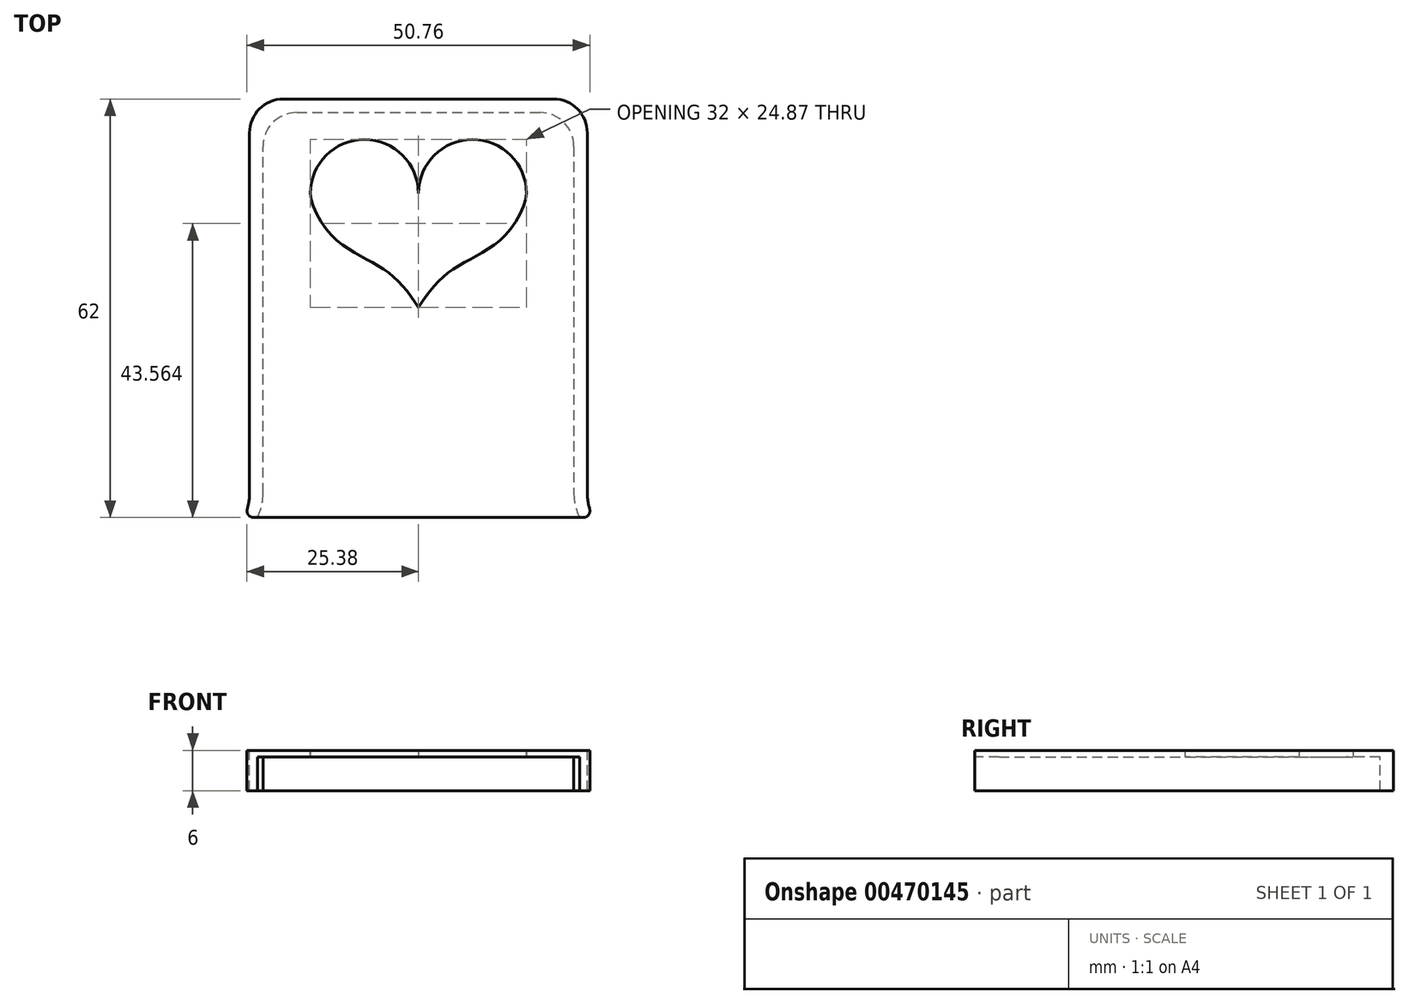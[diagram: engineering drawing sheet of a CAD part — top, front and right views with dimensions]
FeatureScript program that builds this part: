
annotation { "Feature Type Name" : "Feature", "Feature Type Description" : "" }
export const myFeature = defineFeature(function(context is Context, id is Id, definition is map)
    precondition{}
    {
        {
            var Q0;
            Q0=qCreatedBy(makeId("Top.planeOp"),FACE);
            var sketch = newSketch(context, id + "F0", { "sketchPlane" : qUnion([Q0])});
            skLineSegment(sketch, "E0", {"start": v(-23, 30) * mm, "end": v(23, 30) * mm});
            skLineSegment(sketch, "E1", {"start": v(23, 30) * mm, "end": v(23, -30) * mm});
            skLineSegment(sketch, "E2", {"start": v(23, -30) * mm, "end": v(-23, -30) * mm});
            skLineSegment(sketch, "E3", {"start": v(-23, -30) * mm, "end": v(-23, 30) * mm});
            skLineSegment(sketch, "E4", {"start": v(23, 30) * mm, "end": v(-23, -30) * mm, "construction": true});
            skLineSegment(sketch, "E5.MirrorCS", {"start": v(-25.5, -30) * mm, "end": v(-23, -20.3) * mm});
            skLineSegment(sketch, "E6.MirrorCS", {"start": v(-23, -30) * mm, "end": v(-25.5, -30) * mm});
            skLineSegment(sketch, "E7", {"start": v(0, 0) * mm, "end": v(0, 30) * mm, "construction": true});
            skLineSegment(sketch, "E8.MirrorCS", {"start": v(25.5, -30) * mm, "end": v(23, -20.3) * mm});
            skLineSegment(sketch, "E9.MirrorCS", {"start": v(23, -30) * mm, "end": v(25.5, -30) * mm});
            skSolve(sketch);
        }
        {
            var Q0;
            Q0=makeQuery(id+"F0.imprint","IMPRINT",FACE,{"disambiguationData":[TD([[makeQuery(id+"F0.imprint","IMPRINT",EDGE,{"derivedFrom":sQuery(id+"F0.wireOp",EDGE,"E0")}),-1.0]])]});
            var Q1;
            {var subQ2=sQuery(id+"F0.wireOp",EDGE,"E5.MirrorCS");Q1=makeQuery(id+"F0.imprint","IMPRINT",FACE,{"disambiguationData":[TD([[makeQuery(id+"F0.imprint","IMPRINT",EDGE,{"derivedFrom":subQ2}),-1.0]])]});}
            var Q2;
            {var subQ2=sQuery(id+"F0.wireOp",EDGE,"E8.MirrorCS");Q2=makeQuery(id+"F0.imprint","IMPRINT",FACE,{"disambiguationData":[TD([[makeQuery(id+"F0.imprint","IMPRINT",EDGE,{"derivedFrom":subQ2}),1.0]])]});}
            extrude(context, id + "F1", {"entities" : qUnion([Q0, Q1, Q2]), "flatOperationType" : FlatOperationType.REMOVE, "offsetDistance" : 25 * mm, "depth" : 1 * mm, "domain" : OperationDomain.MODEL});
        }
        {
            var Q0;
            Q0=makeQuery(id+"F1.opExtrude","CAP_FACE",FACE,{"disambiguationData":[OSD([sQuery(id+"F0.wireOp",EDGE,"E0"),sQuery(id+"F0.wireOp",EDGE,"E1"),sQuery(id+"F0.wireOp",EDGE,"E2"),sQuery(id+"F0.wireOp",EDGE,"E3")])],"isStart":false});
            var sketch = newSketch(context, id + "F2", { "sketchPlane" : qUnion([Q0])});
            skLineSegment(sketch, "E10", {"start": v(23, -26.4) * mm, "end": v(23, 30) * mm});
            skLineSegment(sketch, "E11", {"start": v(23, 30) * mm, "end": v(0, 30) * mm});
            skLineSegment(sketch, "E12", {"start": v(0, 32) * mm, "end": v(25, 32) * mm});
            skLineSegment(sketch, "E13", {"start": v(25, 32) * mm, "end": v(25, -26.4) * mm});
            skLineSegment(sketch, "E14", {"start": v(23.85, -30) * mm, "end": v(23.85, -30) * mm});
            skLineSegment(sketch, "E15", {"start": v(23.85, -30) * mm, "end": v(25.85, -30) * mm});
            skLineSegment(sketch, "E16", {"start": v(25.85, -30) * mm, "end": v(25.85, -30) * mm});
            skPoint(sketch, "E17.visualSharp", {"position": v(23, -28.3) * mm});
            skArc(sketch, "E17.filletArc", {"start": v(23, -26.4) * mm, "mid": v(23.22, -28.25) * mm, "end": v(23.85, -30) * mm});
            skPoint(sketch, "E18.visualSharp", {"position": v(25, -28.3) * mm});
            skArc(sketch, "E18.filletArc", {"start": v(25, -26.4) * mm, "mid": v(25.22, -28.25) * mm, "end": v(25.85, -30) * mm});
            skLineSegment(sketch, "E19", {"start": v(0, 0) * mm, "end": v(0, 30) * mm, "construction": true});
            skLineSegment(sketch, "E20.MirrorCS", {"start": v(-23.85, -30) * mm, "end": v(-23.85, -30) * mm});
            skArc(sketch, "E21.MirrorCS", {"start": v(-23, -26.4) * mm, "mid": v(-23.22, -28.25) * mm, "end": v(-23.85, -30) * mm});
            skLineSegment(sketch, "E22.MirrorCS", {"start": v(-25.85, -30) * mm, "end": v(-25.85, -30) * mm});
            skArc(sketch, "E23.MirrorCS", {"start": v(-25, -26.4) * mm, "mid": v(-25.22, -28.25) * mm, "end": v(-25.85, -30) * mm});
            skLineSegment(sketch, "E24.MirrorCS", {"start": v(-23.85, -30) * mm, "end": v(-25.85, -30) * mm});
            skPoint(sketch, "E25.MirrorP", {"position": v(-25, -28.3) * mm});
            skLineSegment(sketch, "E26.MirrorCS", {"start": v(0, 32) * mm, "end": v(-25, 32) * mm});
            skLineSegment(sketch, "E27.MirrorCS", {"start": v(-23, -26.4) * mm, "end": v(-23, 30) * mm});
            skLineSegment(sketch, "E28.MirrorCS", {"start": v(-23, 30) * mm, "end": v(0, 30) * mm});
            skLineSegment(sketch, "E29.MirrorCS", {"start": v(-25, 32) * mm, "end": v(-25, -26.4) * mm});
            skPoint(sketch, "E30.MirrorP", {"position": v(-23, -28.3) * mm});
            skSolve(sketch);
        }
        {
            var Q0;
            Q0 = qSketchRegion(id + "F2", true);
            extrude(context, id + "F3", {"entities" : qUnion([Q0]), "operationType" : NewBodyOperationType.ADD, "oppositeDirection" : true, "depth" : 6 * mm});
        }
        {
            var Q0;
            Q0=makeQuery(id+"F3.opExtrude","SWEPT_EDGE",EDGE,{"disambiguationData":[OSD([sQuery(id+"F2.wireOp",EDGE,"E22.MirrorCS"),sQuery(id+"F2.wireOp",EDGE,"E24.MirrorCS")])]});
            var Q1;
            Q1=makeQuery(id+"F3.opExtrude","SWEPT_EDGE",EDGE,{"disambiguationData":[OSD([sQuery(id+"F2.wireOp",EDGE,"E15"),sQuery(id+"F2.wireOp",EDGE,"E16")])]});
            fillet(context, id + "F4", {"entities" : qUnion([Q0, Q1]), "radius" : 1 * mm, "tangentPropagation" : true, "allowEdgeOverflow" : false});
        }
        {
            var Q0;
            Q0=makeQuery(id+"F3.opExtrude","SWEPT_EDGE",EDGE,{"disambiguationData":[OSD([sQuery(id+"F2.wireOp",EDGE,"E10"),sQuery(id+"F2.wireOp",EDGE,"E11")])]});
            var Q1;
            Q1=makeQuery(id+"F3.opExtrude","SWEPT_EDGE",EDGE,{"disambiguationData":[OSD([sQuery(id+"F2.wireOp",EDGE,"E12"),sQuery(id+"F2.wireOp",EDGE,"E13")])]});
            var Q2;
            Q2=makeQuery(id+"F3.opExtrude","SWEPT_EDGE",EDGE,{"disambiguationData":[OSD([sQuery(id+"F2.wireOp",EDGE,"E26.MirrorCS"),sQuery(id+"F2.wireOp",EDGE,"E29.MirrorCS")])]});
            var Q3;
            Q3=makeQuery(id+"F3.opExtrude","SWEPT_EDGE",EDGE,{"disambiguationData":[OSD([sQuery(id+"F2.wireOp",EDGE,"E27.MirrorCS"),sQuery(id+"F2.wireOp",EDGE,"E28.MirrorCS")])]});
            fillet(context, id + "F5", {"entities" : qUnion([Q0, Q1, Q2, Q3]), "radius" : 5 * mm, "tangentPropagation" : true, "allowEdgeOverflow" : false});
        }
        {
            var Q0;
            Q0=makeQuery(id+"F1.opExtrude","CAP_FACE",FACE,{"disambiguationData":[OSD([sQuery(id+"F0.wireOp",EDGE,"E0"),sQuery(id+"F0.wireOp",EDGE,"E1"),sQuery(id+"F0.wireOp",EDGE,"E2"),sQuery(id+"F0.wireOp",EDGE,"E3"),sQuery(id+"F0.wireOp",EDGE,"ucTv49aQ-58Fh-MB05-3OkK-iMjQsQtgxZcr"),sQuery(id+"F0.wireOp",EDGE,"HR3CxZTj-9KNa-pOoI-pPEb-q9pz9odpttWS"),sQuery(id+"F0.wireOp",EDGE,"E5.MirrorCS"),sQuery(id+"F0.wireOp",EDGE,"E6.MirrorCS")])],"isStart":true});
            var sketch = newSketch(context, id + "F6", { "sketchPlane" : qUnion([Q0])});
            skLineSegment(sketch, "E31", {"start": v(23, 0) * mm, "end": v(-23, 0) * mm, "construction": true});
            skLineSegment(sketch, "E32", {"start": v(0, -30) * mm, "end": v(0, 30) * mm, "construction": true});
            skArc(sketch, "E33", {"start": v(-16, 0) * mm, "mid": v(-8, -8) * mm, "end": v(0, 0) * mm});
            skArc(sketch, "E34.MirrorCS", {"start": v(16, 0) * mm, "mid": v(8, -8) * mm, "end": v(0, 0) * mm});
            skFitSpline(sketch, "E35", {"points": [v(-16, 0) * mm, v(-13.57, 5.36) * mm, v(-9.49, 8.72) * mm, v(-5.6, 10.93) * mm, v(-2.6, 13.4) * mm, v(0, 16.87) * mm], "startDerivative": vector(-0.42, 17.18) * mm, "endDerivative": vector(10.54, 16.94) * mm});
            skFitSpline(sketch, "E36.MirrorCS", {"points": [v(16, 0) * mm, v(13.57, 5.36) * mm, v(9.49, 8.72) * mm, v(5.6, 10.93) * mm, v(2.6, 13.4) * mm, v(0, 16.87) * mm], "startDerivative": vector(0.42, 17.18) * mm, "endDerivative": vector(-10.54, 16.94) * mm});
            skSolve(sketch);
        }
        {
            var Q0;
            Q0=makeQuery(id+"F6.imprint","IMPRINT",FACE,{"disambiguationData":[TD([[makeQuery(id+"F6.imprint","IMPRINT",EDGE,{"derivedFrom":sQuery(id+"F6.wireOp",EDGE,"E33")}),1.0]])]});
            extrude(context, id + "F7", {"entities" : qUnion([Q0]), "oppositeDirection" : true, "depth" : 25 * mm, "symmetric" : true});
        }
        {
            var Q0;
            Q0=makeQuery(id+"F7.opExtrude","SWEPT_BODY",BODY,{"disambiguationData":[OSD([sQuery(id+"F6.wireOp",EDGE,"E33"),sQuery(id+"F6.wireOp",EDGE,"E34.MirrorCS"),sQuery(id+"F6.wireOp",EDGE,"E35"),sQuery(id+"F6.wireOp",EDGE,"E36.MirrorCS")])]});
            transform(context, id + "F8", {"entities" : qUnion([Q0]), "transformType" : TransformType.TRANSLATION_3D, "dx" : 0 * mm, "dy" : 18 * mm, "dz" : 0 * mm, "makeCopy" : false});
        }
        {
            var Q0;
            Q0=makeQuery(id+"F7.opExtrude","SWEPT_BODY",BODY,{"disambiguationData":[OSD([sQuery(id+"F6.wireOp",EDGE,"E33"),sQuery(id+"F6.wireOp",EDGE,"E34.MirrorCS"),sQuery(id+"F6.wireOp",EDGE,"E35"),sQuery(id+"F6.wireOp",EDGE,"E36.MirrorCS")])]});
            var Q1;
            Q1=makeQuery(id+"F1.opExtrude","SWEPT_BODY",BODY,{"disambiguationData":[OSD([sQuery(id+"F0.wireOp",EDGE,"E0"),sQuery(id+"F0.wireOp",EDGE,"E1"),sQuery(id+"F0.wireOp",EDGE,"E2"),sQuery(id+"F0.wireOp",EDGE,"E3"),sQuery(id+"F0.wireOp",EDGE,"E5.MirrorCS"),sQuery(id+"F0.wireOp",EDGE,"E6.MirrorCS"),sQuery(id+"F0.wireOp",EDGE,"E8.MirrorCS"),sQuery(id+"F0.wireOp",EDGE,"E9.MirrorCS")])]});
            booleanBodies(context, id + "F9", {"operationType" : BooleanOperationType.SUBTRACTION, "tools" : qUnion([Q0]), "targets" : qUnion([Q1])});
        }
    });
